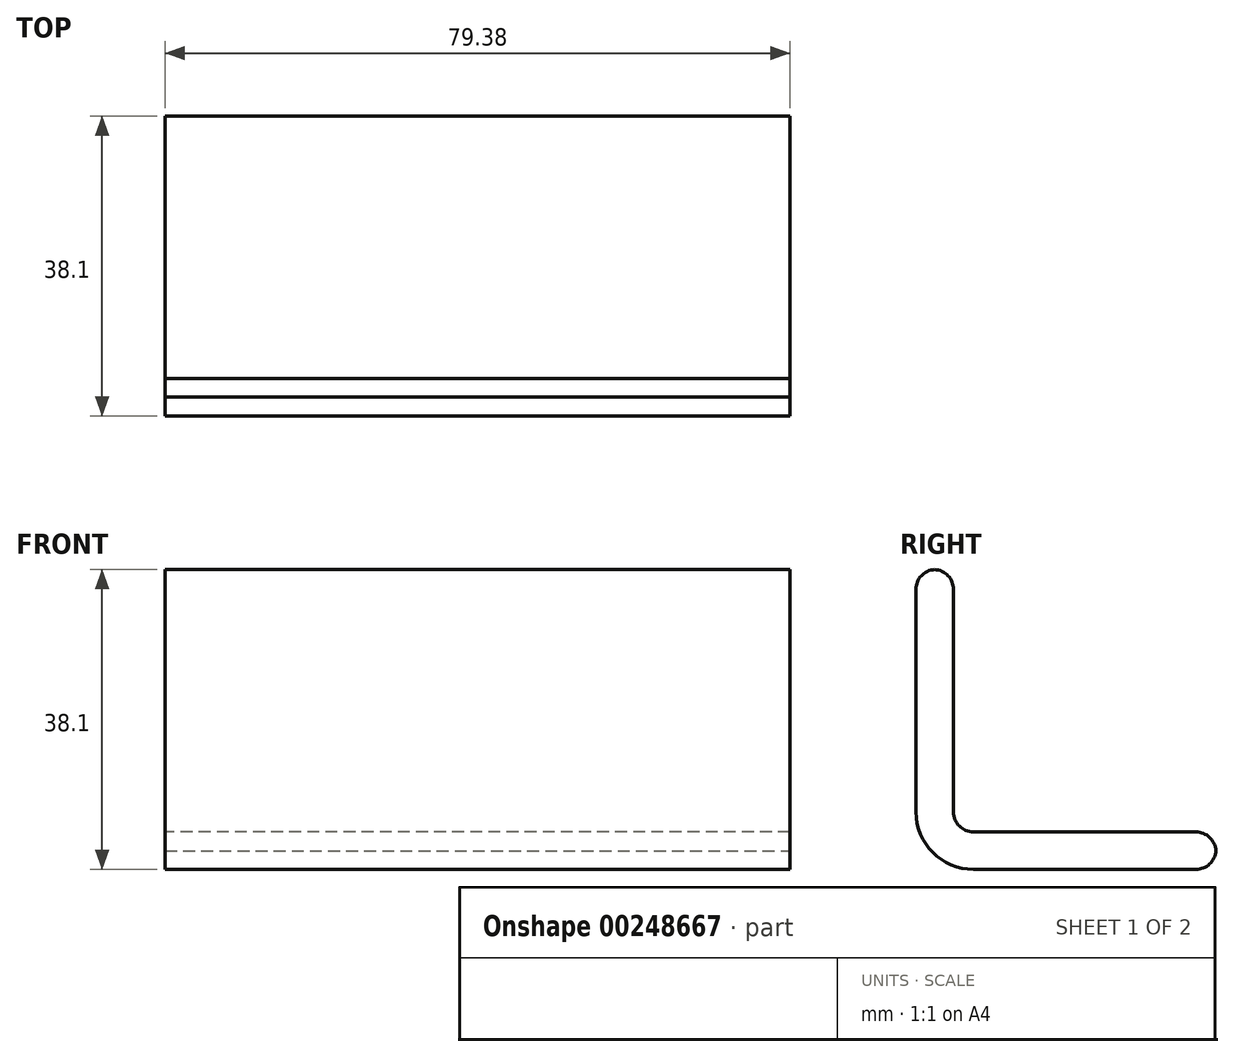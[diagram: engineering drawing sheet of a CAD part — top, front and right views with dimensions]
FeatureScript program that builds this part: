
annotation { "Feature Type Name" : "Feature", "Feature Type Description" : "" }
export const myFeature = defineFeature(function(context is Context, id is Id, definition is map)
    precondition{}
    {
        {
            var Q0;
            Q0=qCreatedBy(makeId("Right.planeOp"),FACE);
            var sketch = newSketch(context, id + "F0", { "sketchPlane" : qUnion([Q0])});
            skLineSegment(sketch, "E0.bottom", {"start": v(0, 0) * mm, "end": v(38.1, 0) * mm});
            skLineSegment(sketch, "E0.top", {"start": v(0, 38.1) * mm, "end": v(4.76, 38.1) * mm});
            skLineSegment(sketch, "E0.left", {"start": v(0, 0) * mm, "end": v(0, 38.1) * mm});
            skLineSegment(sketch, "E0.right", {"start": v(38.1, 0) * mm, "end": v(38.1, 4.76) * mm});
            skLineSegment(sketch, "E1.0", {"start": v(4.76, 4.76) * mm, "end": v(4.76, 38.1) * mm});
            skLineSegment(sketch, "E1.1", {"start": v(4.76, 4.76) * mm, "end": v(38.1, 4.76) * mm});
            skSolve(sketch);
        }
        {
            var Q0;
            Q0 = qSketchRegion(id + "F0", true);
            extrude(context, id + "F1", {"entities" : qUnion([Q0]), "depth" : 79.38 * mm});
        }
        {
            var Q0;
            Q0=makeQuery(id+"F1.opExtrude","SWEPT_EDGE",EDGE,{"disambiguationData":[OSD([sQuery(id+"F0.wireOp",EDGE,"E1.0"),sQuery(id+"F0.wireOp",EDGE,"E1.1")])]});
            var Q1;
            Q1=makeQuery(id+"F1.opExtrude","SWEPT_EDGE",EDGE,{"disambiguationData":[OSD([sQuery(id+"F0.wireOp",EDGE,"E0.top"),sQuery(id+"F0.wireOp",EDGE,"E1.0")])]});
            var Q2;
            Q2=makeQuery(id+"F1.opExtrude","SWEPT_EDGE",EDGE,{"disambiguationData":[OSD([sQuery(id+"F0.wireOp",EDGE,"E0.top"),sQuery(id+"F0.wireOp",EDGE,"E0.left")])]});
            var Q3;
            Q3=makeQuery(id+"F1.opExtrude","SWEPT_EDGE",EDGE,{"disambiguationData":[OSD([sQuery(id+"F0.wireOp",EDGE,"E0.right"),sQuery(id+"F0.wireOp",EDGE,"E1.1")])]});
            var Q4;
            Q4=makeQuery(id+"F1.opExtrude","SWEPT_EDGE",EDGE,{"disambiguationData":[OSD([sQuery(id+"F0.wireOp",EDGE,"E0.bottom"),sQuery(id+"F0.wireOp",EDGE,"E0.right")])]});
            fillet(context, id + "F2", {"entities" : qUnion([Q0, Q1, Q2, Q3, Q4]), "radius" : 2.54 * mm, "tangentPropagation" : true, "allowEdgeOverflow" : false});
        }
        {
            var Q0;
            Q0=makeQuery(id+"F1.opExtrude","SWEPT_EDGE",EDGE,{"disambiguationData":[OSD([sQuery(id+"F0.wireOp",EDGE,"E0.bottom"),sQuery(id+"F0.wireOp",EDGE,"E0.left")])]});
            fillet(context, id + "F3", {"entities" : qUnion([Q0]), "radius" : 7.3 * mm, "tangentPropagation" : true, "allowEdgeOverflow" : false});
        }
    });
